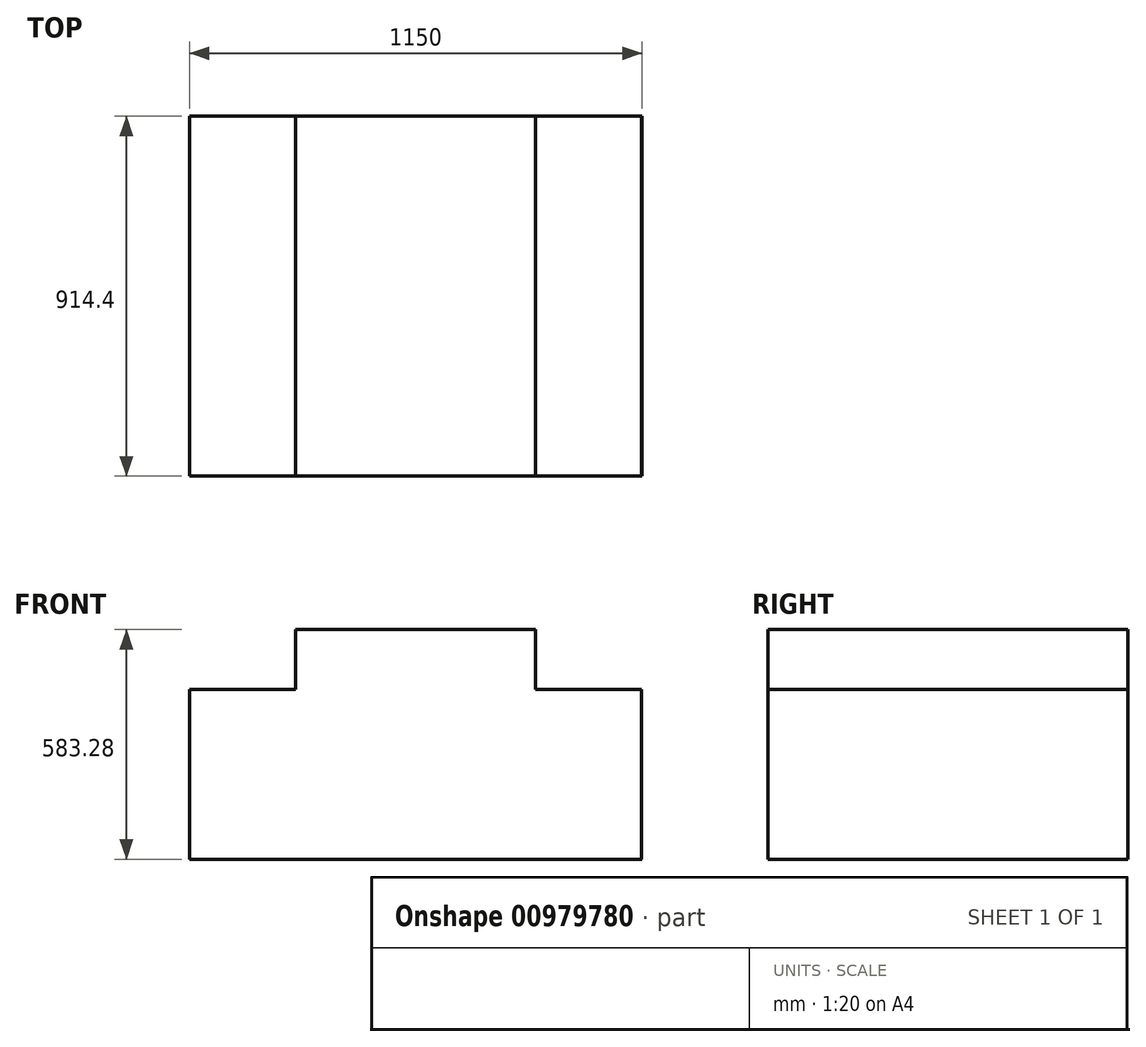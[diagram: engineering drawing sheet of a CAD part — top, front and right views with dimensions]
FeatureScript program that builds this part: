
annotation { "Feature Type Name" : "Feature", "Feature Type Description" : "" }
export const myFeature = defineFeature(function(context is Context, id is Id, definition is map)
    precondition{}
    {
        {
            var Q0;
            Q0=qCreatedBy(makeId("Front.planeOp"),FACE);
            var sketch = newSketch(context, id + "F0", { "sketchPlane" : qUnion([Q0])});
            skLineSegment(sketch, "E0", {"start": v(0, 0) * mm, "end": v(0, 430.88) * mm});
            skLineSegment(sketch, "E1", {"start": v(0, 430.88) * mm, "end": v(269.66, 430.88) * mm});
            skLineSegment(sketch, "E2", {"start": v(269.66, 430.88) * mm, "end": v(269.66, 583.28) * mm});
            skLineSegment(sketch, "E3", {"start": v(269.66, 583.28) * mm, "end": v(574.46, 583.28) * mm});
            skLineSegment(sketch, "E4", {"start": v(574.46, 583.28) * mm, "end": v(574.46, -293.54) * mm, "construction": true});
            skLineSegment(sketch, "E5.MirrorCS", {"start": v(1148.92, 0) * mm, "end": v(1148.92, 430.88) * mm});
            skLineSegment(sketch, "E6.MirrorCS", {"start": v(879.26, 583.28) * mm, "end": v(574.46, 583.28) * mm});
            skLineSegment(sketch, "E7.MirrorCS", {"start": v(1148.92, 430.88) * mm, "end": v(879.26, 430.88) * mm});
            skLineSegment(sketch, "E8.MirrorCS", {"start": v(879.26, 430.88) * mm, "end": v(879.26, 583.28) * mm});
            skSolve(sketch);
        }
        {
            var Q0;
            Q0=sQuery(id+"F0.wireOp",EDGE,"E0");
            var Q1;
            Q1=sQuery(id+"F0.wireOp",EDGE,"E8.MirrorCS");
            var Q2;
            Q2=sQuery(id+"F0.wireOp",EDGE,"E7.MirrorCS");
            var Q3;
            Q3=sQuery(id+"F0.wireOp",EDGE,"E5.MirrorCS");
            var Q4;
            Q4=sQuery(id+"F0.wireOp",EDGE,"E3");
            var Q5;
            Q5=sQuery(id+"F0.wireOp",EDGE,"E6.MirrorCS");
            var Q6;
            Q6=sQuery(id+"F0.wireOp",EDGE,"E1");
            var Q7;
            Q7=sQuery(id+"F0.wireOp",EDGE,"E2");
            extrude(context, id + "F1", {"bodyType" : ToolBodyType.SURFACE, "surfaceEntities" : qUnion([Q0, Q1, Q2, Q3, Q4, Q5, Q6, Q7]), "depth" : 914.4 * mm, "offsetDistance" : 30.48 * mm});
        }
        {
            var Q0;
            Q0=qCreatedBy(makeId("Front.planeOp"),FACE);
            var sketch = newSketch(context, id + "F2", { "sketchPlane" : qUnion([Q0])});
            skLineSegment(sketch, "E9", {"start": v(0, 0) * mm, "end": v(1150, 0) * mm});
            skSolve(sketch);
        }
        {
            var Q0;
            Q0=sQuery(id+"F2.wireOp",EDGE,"E9");
            extrude(context, id + "F3", {"bodyType" : ToolBodyType.SURFACE, "surfaceEntities" : qUnion([Q0]), "depth" : 914.4 * mm, "offsetDistance" : 30.48 * mm});
        }
    });
